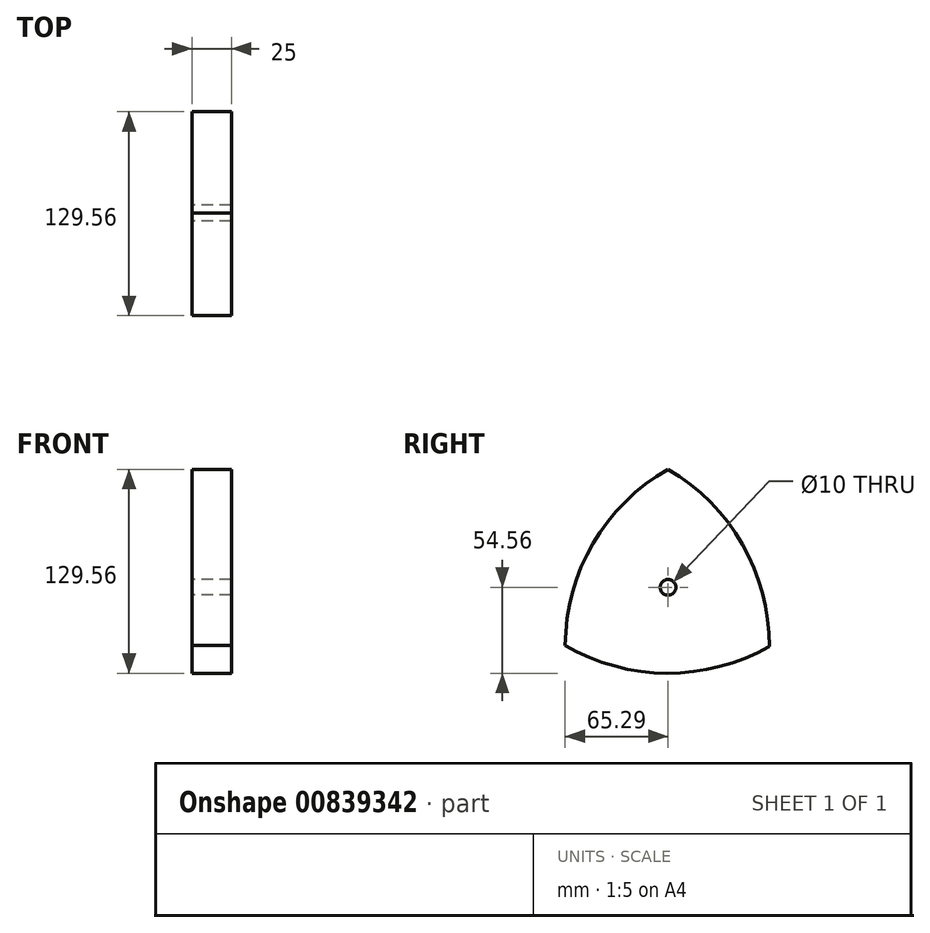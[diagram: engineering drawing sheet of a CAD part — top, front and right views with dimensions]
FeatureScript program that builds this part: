
annotation { "Feature Type Name" : "Feature", "Feature Type Description" : "" }
export const myFeature = defineFeature(function(context is Context, id is Id, definition is map)
    precondition{}
    {
        {
            var Q0;
            Q0=qCreatedBy(makeId("Right.planeOp"),FACE);
            var sketch = newSketch(context, id + "F0", { "sketchPlane" : qUnion([Q0])});
            skLineSegment(sketch, "E0", {"start": v(64.27, -37.5) * mm, "end": v(0, 75) * mm, "construction": true});
            skLineSegment(sketch, "E1.MirrorCS", {"start": v(-65.3, -36.9) * mm, "end": v(0, 75) * mm, "construction": true});
            skArc(sketch, "E2", {"start": v(0, 75) * mm, "mid": v(-47.64, 27.8) * mm, "end": v(-65.3, -36.9) * mm});
            skArc(sketch, "E3", {"start": v(64.27, -37.5) * mm, "mid": v(47.2, 27.36) * mm, "end": v(0, 75) * mm});
            skArc(sketch, "E4", {"start": v(-65.3, -36.9) * mm, "mid": v(-0.59, -54.56) * mm, "end": v(64.27, -37.5) * mm});
            skPoint(sketch, "E5", {"position": v(-47.64, 27.8) * mm});
            skPoint(sketch, "E6", {"position": v(47.2, 27.36) * mm});
            skPoint(sketch, "E7", {"position": v(-0.59, -54.56) * mm});
            skLineSegment(sketch, "E8", {"start": v(-47.64, 27.8) * mm, "end": v(0, 0) * mm, "construction": true});
            skLineSegment(sketch, "E9", {"start": v(0, 0) * mm, "end": v(47.2, 27.36) * mm, "construction": true});
            skCircle(sketch, "E10", {"center": v(0, 0) * mm, "radius": 5 * mm});
            skLineSegment(sketch, "E11", {"start": v(-65.3, -36.9) * mm, "end": v(64.27, -37.5) * mm, "construction": true});
            skLineSegment(sketch, "E12", {"start": v(0, 0) * mm, "end": v(-0.59, -54.56) * mm, "construction": true});
            skSolve(sketch);
        }
        {
            var Q0;
            Q0 = qSketchRegion(id + "F0", true);
            extrude(context, id + "F1", {"entities" : qUnion([Q0]), "depth" : 25 * mm, "offsetDistance" : 25 * mm});
        }
    });
